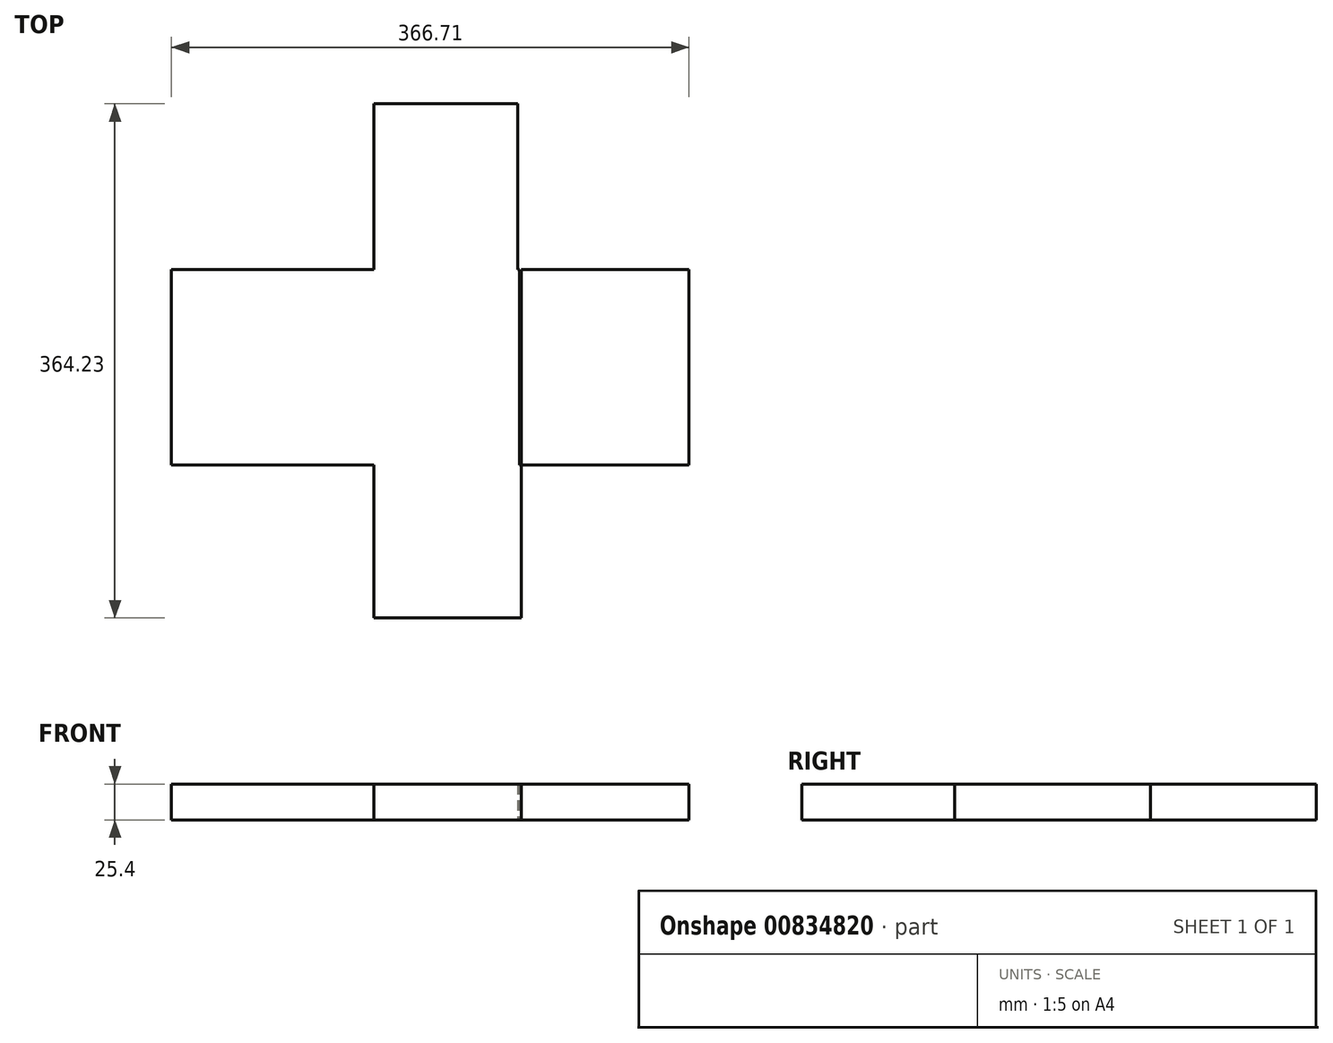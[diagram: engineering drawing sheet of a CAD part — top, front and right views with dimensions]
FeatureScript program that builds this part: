
annotation { "Feature Type Name" : "Feature", "Feature Type Description" : "" }
export const myFeature = defineFeature(function(context is Context, id is Id, definition is map)
    precondition{}
    {
        {
            var Q0;
            Q0=qCreatedBy(makeId("Top.planeOp"),FACE);
            var sketch = newSketch(context, id + "F0", { "sketchPlane" : qUnion([Q0])});
            skLineSegment(sketch, "E0.bottom", {"start": v(-213.3, -58.9) * mm, "end": v(-70, -58.9) * mm});
            skLineSegment(sketch, "E0.top", {"start": v(-213.3, -8.56) * mm, "end": v(-70, -8.56) * mm});
            skLineSegment(sketch, "E0.left", {"start": v(-213.3, -58.9) * mm, "end": v(-213.3, -8.56) * mm});
            skLineSegment(sketch, "E0.right", {"start": v(-70, -58.9) * mm, "end": v(-70, -8.56) * mm});
            skLineSegment(sketch, "E1.top", {"start": v(-213.3, -147.14) * mm, "end": v(-70, -147.14) * mm});
            skLineSegment(sketch, "E1.left", {"start": v(-213.3, -58.9) * mm, "end": v(-213.3, -147.14) * mm});
            skLineSegment(sketch, "E1.right", {"start": v(-70, -58.9) * mm, "end": v(-70, -147.14) * mm});
            skLineSegment(sketch, "E2.bottom", {"start": v(-70, -8.56) * mm, "end": v(33.23, -8.56) * mm});
            skLineSegment(sketch, "E2.top", {"start": v(-70, -147.14) * mm, "end": v(33.23, -147.14) * mm});
            skLineSegment(sketch, "E2.left", {"start": v(-70, -8.56) * mm, "end": v(-70, -147.14) * mm});
            skLineSegment(sketch, "E2.right", {"start": v(33.23, -8.56) * mm, "end": v(33.23, -147.14) * mm});
            skLineSegment(sketch, "E3.bottom", {"start": v(-70, -147.14) * mm, "end": v(34.38, -147.14) * mm});
            skLineSegment(sketch, "E3.top", {"start": v(-70, -255.4) * mm, "end": v(34.38, -255.4) * mm});
            skLineSegment(sketch, "E3.left", {"start": v(-70, -147.14) * mm, "end": v(-70, -255.4) * mm});
            skLineSegment(sketch, "E3.right", {"start": v(34.38, -147.14) * mm, "end": v(34.38, -255.4) * mm});
            skLineSegment(sketch, "E4.bottom", {"start": v(-70, -8.56) * mm, "end": v(31.97, -8.56) * mm});
            skLineSegment(sketch, "E4.top", {"start": v(-70, 108.82) * mm, "end": v(31.97, 108.82) * mm});
            skLineSegment(sketch, "E4.left", {"start": v(-70, -8.56) * mm, "end": v(-70, 108.82) * mm});
            skLineSegment(sketch, "E4.right", {"start": v(31.97, -8.56) * mm, "end": v(31.97, 108.82) * mm});
            skLineSegment(sketch, "E5.bottom", {"start": v(34.38, -147.14) * mm, "end": v(153.4, -147.14) * mm});
            skLineSegment(sketch, "E5.top", {"start": v(34.38, -8.56) * mm, "end": v(153.4, -8.56) * mm});
            skLineSegment(sketch, "E5.left", {"start": v(34.38, -147.14) * mm, "end": v(34.38, -8.56) * mm});
            skLineSegment(sketch, "E5.right", {"start": v(153.4, -147.14) * mm, "end": v(153.4, -8.56) * mm});
            skSolve(sketch);
        }
        {
            var Q0;
            Q0 = qSketchRegion(id + "F0", true);
            extrude(context, id + "F1", {"entities" : qUnion([Q0]), "depth" : 25.4 * mm, "offsetDistance" : 25.4 * mm});
        }
    });
